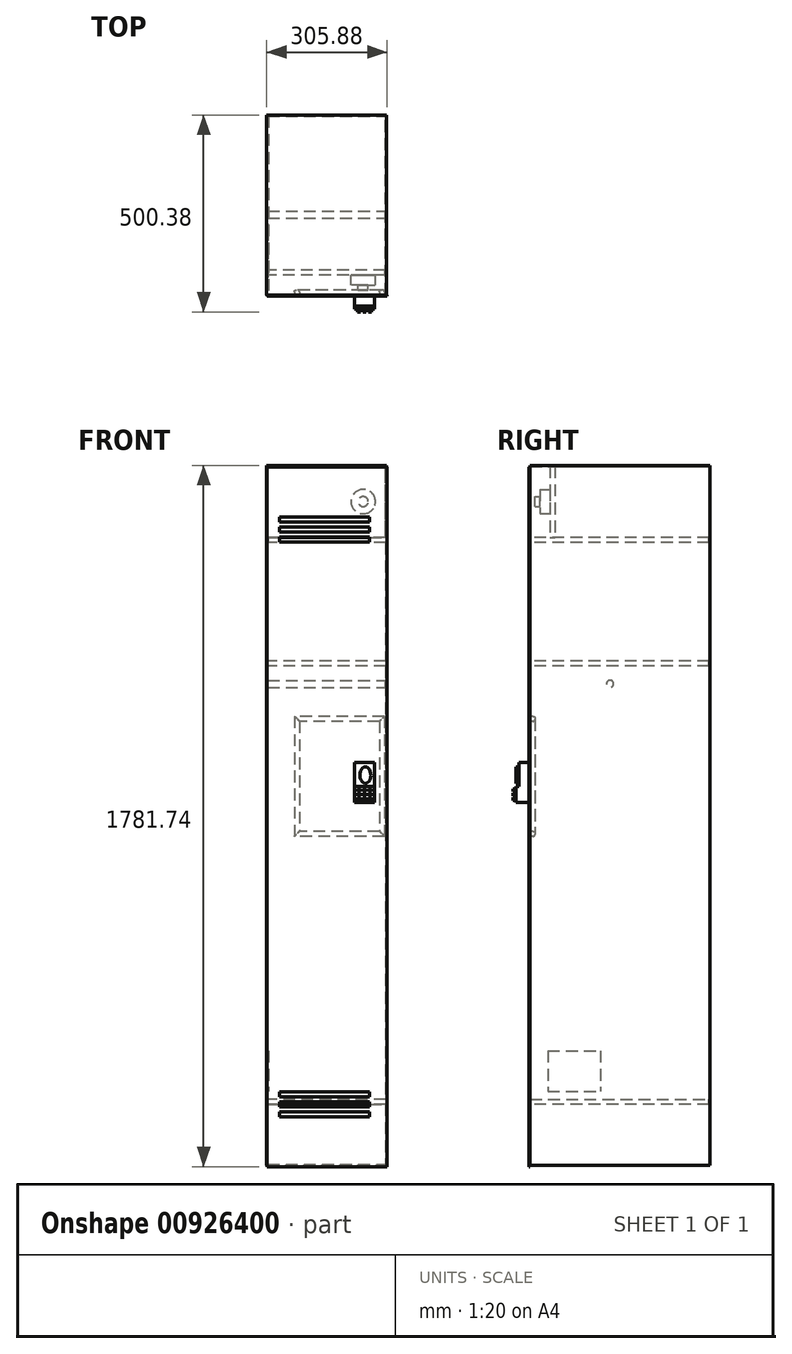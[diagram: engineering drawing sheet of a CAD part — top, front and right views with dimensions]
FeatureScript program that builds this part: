
annotation { "Feature Type Name" : "Feature", "Feature Type Description" : "" }
export const myFeature = defineFeature(function(context is Context, id is Id, definition is map)
    precondition{}
    {
        {
            var Q0;
            Q0=qCreatedBy(makeId("Front.planeOp"),FACE);
            var sketch = newSketch(context, id + "F0", { "sketchPlane" : qUnion([Q0])});
            skLineSegment(sketch, "E0.bottom", {"start": v(-28.78, 1709) * mm, "end": v(276.02, 1709) * mm});
            skLineSegment(sketch, "E0.top", {"start": v(-28.78, -69) * mm, "end": v(276.02, -69) * mm});
            skLineSegment(sketch, "E0.left", {"start": v(-28.78, 1709) * mm, "end": v(-28.78, -69) * mm});
            skLineSegment(sketch, "E0.right", {"start": v(276.02, 1709) * mm, "end": v(276.02, -69) * mm});
            skPoint(sketch, "E1", {"position": v(-28.78, 1709) * mm});
            skPoint(sketch, "E2", {"position": v(-28.78, -69) * mm});
            skSolve(sketch);
        }
        {
            var Q0;
            Q0=qSketchRegion(id+"F0",true);
            extrude(context, id + "F1", {"entities" : qUnion([Q0]), "depth" : 457.2 * mm, "offsetDistance" : 25.4 * mm});
        }
        {
            var Q0;
            Q0=makeQuery(id+"F1.opExtrude","CAP_FACE",FACE,{"disambiguationData":[OSD([sQuery(id+"F0.wireOp",EDGE,"E0.bottom"),sQuery(id+"F0.wireOp",EDGE,"E0.top"),sQuery(id+"F0.wireOp",EDGE,"E0.left"),sQuery(id+"F0.wireOp",EDGE,"E0.right")])],"isStart":false});
            shell(context, id + "F2", {"entities" : qUnion([Q0]), "thickness" : 2.54 * mm});
        }
        {
            var Q0;
            Q0=makeQuery(id+"F2.opShell","OFFSET_FACE",FACE,{"disambiguationData":[OSD([sQuery(id+"F0.wireOp",EDGE,"E0.left")])]});
            var sketch = newSketch(context, id + "F3", { "sketchPlane" : qUnion([Q0])});
            skPoint(sketch, "E3", {"position": v(-457.2, 1706.45) * mm});
            skPoint(sketch, "E4", {"position": v(-457.2, -66.47) * mm});
            skSolve(sketch);
        }
        {
            var Q0;
            Q0=qCreatedBy(makeId("Front.planeOp"),FACE);
            cPlane(context, id + "F4", {"entities" : qUnion([Q0]), "cplaneType" : CPlaneType.OFFSET, "offset" : 457.2 * mm, "width" : 152.4 * mm, "height" : 152.4 * mm});
        }
        {
            var Q0;
            Q0=qCreatedBy(id+"F4.planeOp",FACE);
            var sketch = newSketch(context, id + "F5", { "sketchPlane" : qUnion([Q0])});
            skLineSegment(sketch, "E5.bottom", {"start": v(-26.2, 98.63) * mm, "end": v(273.47, 98.63) * mm});
            skLineSegment(sketch, "E5.top", {"start": v(-26.2, 85.93) * mm, "end": v(273.47, 85.93) * mm});
            skLineSegment(sketch, "E5.left", {"start": v(-26.2, 98.63) * mm, "end": v(-26.2, 85.93) * mm});
            skLineSegment(sketch, "E5.right", {"start": v(273.47, 98.63) * mm, "end": v(273.47, 85.93) * mm});
            skLineSegment(sketch, "E6.bottom", {"start": v(-25, 1211.53) * mm, "end": v(273.53, 1211.53) * mm});
            skLineSegment(sketch, "E6.top", {"start": v(-25, 1198.83) * mm, "end": v(273.53, 1198.83) * mm});
            skLineSegment(sketch, "E6.left", {"start": v(-25, 1211.53) * mm, "end": v(-25, 1198.83) * mm});
            skLineSegment(sketch, "E6.right", {"start": v(273.53, 1211.53) * mm, "end": v(273.53, 1198.83) * mm});
            skLineSegment(sketch, "E7.bottom", {"start": v(-24.41, 1525.34) * mm, "end": v(273.53, 1525.34) * mm});
            skLineSegment(sketch, "E7.top", {"start": v(-24.41, 1512.64) * mm, "end": v(273.53, 1512.64) * mm});
            skLineSegment(sketch, "E7.left", {"start": v(-24.41, 1525.34) * mm, "end": v(-24.41, 1512.64) * mm});
            skLineSegment(sketch, "E7.right", {"start": v(273.53, 1525.34) * mm, "end": v(273.53, 1512.64) * mm});
            skSolve(sketch);
        }
        {
            var Q0;
            Q0=makeQuery(id+"F5.imprint","IMPRINT",FACE,{"disambiguationData":[TD([[makeQuery(id+"F5.imprint","IMPRINT",EDGE,{"derivedFrom":sQuery(id+"F5.wireOp",EDGE,"E5.bottom")}),-1.0]])]});
            var Q1;
            Q1=makeQuery(id+"F5.imprint","IMPRINT",FACE,{"disambiguationData":[TD([[makeQuery(id+"F5.imprint","IMPRINT",EDGE,{"derivedFrom":sQuery(id+"F5.wireOp",EDGE,"VyrBGK2K-1y9x-VAEc-Igx1-qJqO2NATqdDI.bottom")}),-1.0]])]});
            var Q2;
            Q2=makeQuery(id+"F5.imprint","IMPRINT",FACE,{"disambiguationData":[TD([[makeQuery(id+"F5.imprint","IMPRINT",EDGE,{"derivedFrom":sQuery(id+"F5.wireOp",EDGE,"E6.bottom")}),-1.0]])]});
            var Q3;
            Q3=makeQuery(id+"F5.imprint","IMPRINT",FACE,{"disambiguationData":[TD([[makeQuery(id+"F5.imprint","IMPRINT",EDGE,{"derivedFrom":sQuery(id+"F5.wireOp",EDGE,"E7.bottom")}),-1.0]])]});
            extrude(context, id + "F6", {"entities" : qUnion([Q0, Q1, Q2, Q3]), "operationType" : NewBodyOperationType.ADD, "endBound" : BoundingType.UP_TO_NEXT, "oppositeDirection" : true, "depth" : 25.4 * mm, "offsetDistance" : 25.4 * mm});
        }
        {
            var Q0;
            Q0=makeQuery(id+"F6.boolean.opBoolean","MERGE",FACE,{"derivedFrom":[makeQuery(id+"F1.opExtrude","CAP_FACE",FACE,{"disambiguationData":[OSD([sQuery(id+"F0.wireOp",EDGE,"E0.bottom"),sQuery(id+"F0.wireOp",EDGE,"E0.top"),sQuery(id+"F0.wireOp",EDGE,"E0.left"),sQuery(id+"F0.wireOp",EDGE,"E0.right")])],"isStart":false}),makeQuery(id+"F6.opExtrude","CAP_FACE",FACE,{"disambiguationData":[OSD([sQuery(id+"F5.wireOp",EDGE,"E5.bottom"),sQuery(id+"F5.wireOp",EDGE,"E5.top"),sQuery(id+"F5.wireOp",EDGE,"E5.left"),sQuery(id+"F5.wireOp",EDGE,"E5.right")])],"isStart":true}),makeQuery(id+"F6.opExtrude","CAP_FACE",FACE,{"disambiguationData":[OSD([sQuery(id+"F5.wireOp",EDGE,"E6.bottom"),sQuery(id+"F5.wireOp",EDGE,"E6.top"),sQuery(id+"F5.wireOp",EDGE,"E6.left"),sQuery(id+"F5.wireOp",EDGE,"E6.right")])],"isStart":true}),makeQuery(id+"F6.opExtrude","CAP_FACE",FACE,{"disambiguationData":[OSD([sQuery(id+"F5.wireOp",EDGE,"E7.bottom"),sQuery(id+"F5.wireOp",EDGE,"E7.top"),sQuery(id+"F5.wireOp",EDGE,"E7.left"),sQuery(id+"F5.wireOp",EDGE,"E7.right")])],"isStart":true})]});
            var sketch = newSketch(context, id + "F7", { "sketchPlane" : qUnion([Q0])});
            skPoint(sketch, "E8", {"position": v(-25, 1198.83) * mm});
            skPoint(sketch, "E9", {"position": v(273.48, 1198.83) * mm});
            skPoint(sketch, "E10", {"position": v(124.24, 1198.83) * mm});
            skSolve(sketch);
        }
        {
            var Q0;
            {var subQ7=sQuery(id+"F0.wireOp",EDGE,"E0.bottom");var subQ8=makeQuery(id+"F1.opExtrude","CAP_EDGE",EDGE,{"disambiguationData":[OSD([subQ7])],"isStart":false});Q0=makeQuery(id+"F7.imprint","IMPRINT",FACE,{"disambiguationData":[TD([[makeQuery(id+"F7.imprint","IMPRINT",EDGE,{"derivedFrom":subQ8}),-1.0]])]});}
            cPlane(context, id + "F8", {"entities" : qUnion([Q0]), "cplaneType" : CPlaneType.OFFSET, "offset" : 0 * mm, "width" : 152.4 * mm, "height" : 152.4 * mm});
        }
        {
            var Q0;
            Q0=qCreatedBy(id+"F8.planeOp",FACE);
            var sketch = newSketch(context, id + "F9", { "sketchPlane" : qUnion([Q0])});
            skLineSegment(sketch, "E11.bottom", {"start": v(-27.7, 1705.25) * mm, "end": v(277.1, 1705.25) * mm});
            skLineSegment(sketch, "E11.top", {"start": v(-27.7, -72.75) * mm, "end": v(277.1, -72.75) * mm});
            skLineSegment(sketch, "E11.left", {"start": v(-27.7, 1705.25) * mm, "end": v(-27.7, -72.75) * mm});
            skLineSegment(sketch, "E11.right", {"start": v(277.1, 1705.25) * mm, "end": v(277.1, -72.75) * mm});
            skLineSegment(sketch, "E12.bottom", {"start": v(3.97, 1578.25) * mm, "end": v(232.57, 1578.25) * mm});
            skLineSegment(sketch, "E12.top", {"start": v(3.97, 1565.55) * mm, "end": v(232.57, 1565.55) * mm});
            skLineSegment(sketch, "E12.left", {"start": v(3.97, 1578.25) * mm, "end": v(3.97, 1565.55) * mm});
            skLineSegment(sketch, "E12.right", {"start": v(232.57, 1578.25) * mm, "end": v(232.57, 1565.55) * mm});
            skLineSegment(sketch, "E13.bottom", {"start": v(232.57, 1552.85) * mm, "end": v(3.97, 1552.85) * mm});
            skLineSegment(sketch, "E13.top", {"start": v(232.57, 1540.15) * mm, "end": v(3.97, 1540.15) * mm});
            skLineSegment(sketch, "E13.left", {"start": v(232.57, 1552.85) * mm, "end": v(232.57, 1540.15) * mm});
            skLineSegment(sketch, "E13.right", {"start": v(3.97, 1552.85) * mm, "end": v(3.97, 1540.15) * mm});
            skLineSegment(sketch, "E14.bottom", {"start": v(232.57, 1527.45) * mm, "end": v(3.97, 1527.45) * mm});
            skLineSegment(sketch, "E14.top", {"start": v(232.57, 1514.75) * mm, "end": v(3.97, 1514.75) * mm});
            skLineSegment(sketch, "E14.left", {"start": v(232.57, 1527.45) * mm, "end": v(232.57, 1514.75) * mm});
            skLineSegment(sketch, "E14.right", {"start": v(3.97, 1527.45) * mm, "end": v(3.97, 1514.75) * mm});
            skLineSegment(sketch, "E15", {"start": v(203.5, -72.75) * mm, "end": v(203.5, 816.25) * mm, "construction": true});
            skLineSegment(sketch, "E16", {"start": v(277.1, 816.25) * mm, "end": v(-27.7, 816.25) * mm, "construction": true});
            skLineSegment(sketch, "E17.MirrorCS", {"start": v(232.57, 117.75) * mm, "end": v(3.97, 117.75) * mm});
            skLineSegment(sketch, "E18.MirrorCS", {"start": v(232.57, 105.05) * mm, "end": v(3.97, 105.05) * mm});
            skLineSegment(sketch, "E19.MirrorCS", {"start": v(232.57, 92.35) * mm, "end": v(3.97, 92.35) * mm});
            skLineSegment(sketch, "E20.MirrorCS", {"start": v(232.57, 79.65) * mm, "end": v(3.97, 79.65) * mm});
            skLineSegment(sketch, "E21.MirrorCS", {"start": v(3.97, 66.95) * mm, "end": v(232.57, 66.95) * mm});
            skLineSegment(sketch, "E22.MirrorCS", {"start": v(3.97, 54.25) * mm, "end": v(232.57, 54.25) * mm});
            skLineSegment(sketch, "E23.MirrorCS", {"start": v(3.97, 54.25) * mm, "end": v(3.97, 66.95) * mm});
            skLineSegment(sketch, "E24.MirrorCS", {"start": v(3.97, 79.65) * mm, "end": v(3.97, 92.35) * mm});
            skLineSegment(sketch, "E25.MirrorCS", {"start": v(3.97, 105.05) * mm, "end": v(3.97, 117.75) * mm});
            skLineSegment(sketch, "E26.MirrorCS", {"start": v(232.57, 105.05) * mm, "end": v(232.57, 117.75) * mm});
            skLineSegment(sketch, "E27.MirrorCS", {"start": v(232.57, 79.65) * mm, "end": v(232.57, 92.35) * mm});
            skLineSegment(sketch, "E28.MirrorCS", {"start": v(232.57, 54.25) * mm, "end": v(232.57, 66.95) * mm});
            skLineSegment(sketch, "E29", {"start": v(174.02, 54.25) * mm, "end": v(174.02, -72.75) * mm, "construction": true});
            skSolve(sketch);
        }
        {
            var Q0;
            Q0=makeQuery(id+"F9.imprint","IMPRINT",FACE,{"disambiguationData":[TD([[makeQuery(id+"F9.imprint","IMPRINT",EDGE,{"derivedFrom":sQuery(id+"F9.wireOp",EDGE,"E11.bottom")}),-1.0]])]});
            extrude(context, id + "F10", {"entities" : qUnion([Q0]), "operationType" : NewBodyOperationType.ADD, "depth" : 2.54 * mm, "offsetDistance" : 25.4 * mm});
        }
        {
            var Q0;
            Q0=makeQuery(id+"F10.opExtrude","CAP_FACE",FACE,{"disambiguationData":[OSD([sQuery(id+"F9.wireOp",EDGE,"E11.bottom"),sQuery(id+"F9.wireOp",EDGE,"E11.top"),sQuery(id+"F9.wireOp",EDGE,"E11.left"),sQuery(id+"F9.wireOp",EDGE,"E11.right"),sQuery(id+"F9.wireOp",EDGE,"E12.bottom"),sQuery(id+"F9.wireOp",EDGE,"E12.top"),sQuery(id+"F9.wireOp",EDGE,"E12.left"),sQuery(id+"F9.wireOp",EDGE,"E12.right"),sQuery(id+"F9.wireOp",EDGE,"E13.bottom"),sQuery(id+"F9.wireOp",EDGE,"E13.top"),sQuery(id+"F9.wireOp",EDGE,"E13.left"),sQuery(id+"F9.wireOp",EDGE,"E13.right"),sQuery(id+"F9.wireOp",EDGE,"E14.bottom"),sQuery(id+"F9.wireOp",EDGE,"E14.top"),sQuery(id+"F9.wireOp",EDGE,"E14.left"),sQuery(id+"F9.wireOp",EDGE,"E14.right")])],"isStart":false});
            var sketch = newSketch(context, id + "F11", { "sketchPlane" : qUnion([Q0])});
            skLineSegment(sketch, "E30.bottom", {"start": v(195, 953.76) * mm, "end": v(245.8, 953.76) * mm});
            skLineSegment(sketch, "E30.top", {"start": v(195, 852.16) * mm, "end": v(245.8, 852.16) * mm});
            skLineSegment(sketch, "E30.left", {"start": v(195, 953.76) * mm, "end": v(195, 852.16) * mm});
            skLineSegment(sketch, "E30.right", {"start": v(245.8, 953.76) * mm, "end": v(245.8, 852.16) * mm});
            skSolve(sketch);
        }
        {
            var Q0;
            Q0=makeQuery(id+"F11.imprint","IMPRINT",FACE,{"disambiguationData":[TD([[makeQuery(id+"F11.imprint","IMPRINT",EDGE,{"derivedFrom":sQuery(id+"F11.wireOp",EDGE,"E30.bottom")}),-1.0]])]});
            extrude(context, id + "F12", {"entities" : qUnion([Q0]), "operationType" : NewBodyOperationType.ADD, "depth" : 25.4 * mm, "offsetDistance" : 25.4 * mm});
        }
        {
            var Q0;
            {var subQ0=sQuery(id+"F5.wireOp",EDGE,"E5.bottom");var subQ1=sQuery(id+"F0.wireOp",EDGE,"E0.right");Q0=makeQuery(id+"F6.boolean.opBoolean","SPLIT",FACE,{"disambiguationData":[TD([makeQuery(id+"F6.opExtrude","SWEPT_FACE",FACE,{"disambiguationData":[OSD([subQ0])]})])],"derivedFrom":makeQuery(id+"F2.opShell","OFFSET_FACE",FACE,{"disambiguationData":[OSD([subQ1])]})});}
            var sketch = newSketch(context, id + "F13", { "sketchPlane" : qUnion([Q0])});
            skCircle(sketch, "E31", {"center": v(253.8, 1154.02) * mm, "radius": 8.9 * mm});
            skSolve(sketch);
        }
        {
            var Q0;
            Q0=makeQuery(id+"F13.imprint","IMPRINT",FACE,{"disambiguationData":[TD([[makeQuery(id+"F13.imprint","IMPRINT",EDGE,{"derivedFrom":sQuery(id+"F13.wireOp",EDGE,"E31")}),1.0]])]});
            extrude(context, id + "F14", {"entities" : qUnion([Q0]), "operationType" : NewBodyOperationType.ADD, "endBound" : BoundingType.UP_TO_NEXT, "depth" : 25.4 * mm, "offsetDistance" : 25.4 * mm});
        }
        {
            var Q0;
            Q0=makeQuery(id+"F10.opExtrude","CAP_FACE",FACE,{"disambiguationData":[OSD([sQuery(id+"F9.wireOp",EDGE,"E11.bottom"),sQuery(id+"F9.wireOp",EDGE,"E11.top"),sQuery(id+"F9.wireOp",EDGE,"E11.left"),sQuery(id+"F9.wireOp",EDGE,"E11.right"),sQuery(id+"F9.wireOp",EDGE,"E12.bottom"),sQuery(id+"F9.wireOp",EDGE,"E12.top"),sQuery(id+"F9.wireOp",EDGE,"E12.left"),sQuery(id+"F9.wireOp",EDGE,"E12.right"),sQuery(id+"F9.wireOp",EDGE,"E13.bottom"),sQuery(id+"F9.wireOp",EDGE,"E13.top"),sQuery(id+"F9.wireOp",EDGE,"E13.left"),sQuery(id+"F9.wireOp",EDGE,"E13.right"),sQuery(id+"F9.wireOp",EDGE,"E14.bottom"),sQuery(id+"F9.wireOp",EDGE,"E14.top"),sQuery(id+"F9.wireOp",EDGE,"E14.left"),sQuery(id+"F9.wireOp",EDGE,"E14.right"),sQuery(id+"F9.wireOp",EDGE,"E17.MirrorCS"),sQuery(id+"F9.wireOp",EDGE,"E18.MirrorCS"),sQuery(id+"F9.wireOp",EDGE,"E19.MirrorCS"),sQuery(id+"F9.wireOp",EDGE,"E20.MirrorCS"),sQuery(id+"F9.wireOp",EDGE,"E21.MirrorCS"),sQuery(id+"F9.wireOp",EDGE,"E22.MirrorCS"),sQuery(id+"F9.wireOp",EDGE,"E23.MirrorCS"),sQuery(id+"F9.wireOp",EDGE,"E24.MirrorCS"),sQuery(id+"F9.wireOp",EDGE,"E25.MirrorCS"),sQuery(id+"F9.wireOp",EDGE,"E26.MirrorCS"),sQuery(id+"F9.wireOp",EDGE,"E27.MirrorCS"),sQuery(id+"F9.wireOp",EDGE,"E28.MirrorCS")])],"isStart":true});
            var sketch = newSketch(context, id + "F15", { "sketchPlane" : qUnion([Q0])});
            skLineSegment(sketch, "E32.bottom", {"start": v(-270.4, 1071.45) * mm, "end": v(-41.8, 1071.45) * mm});
            skLineSegment(sketch, "E32.top", {"start": v(-270.4, 766.65) * mm, "end": v(-41.8, 766.65) * mm});
            skLineSegment(sketch, "E32.left", {"start": v(-270.4, 1071.45) * mm, "end": v(-270.4, 766.65) * mm});
            skLineSegment(sketch, "E32.right", {"start": v(-41.8, 1071.45) * mm, "end": v(-41.8, 766.65) * mm});
            skLineSegment(sketch, "E33.0", {"start": v(-257.7, 1058.75) * mm, "end": v(-54.5, 1058.75) * mm});
            skLineSegment(sketch, "E33.1", {"start": v(-257.7, 1058.75) * mm, "end": v(-257.7, 779.35) * mm});
            skLineSegment(sketch, "E33.2", {"start": v(-257.7, 779.35) * mm, "end": v(-54.5, 779.35) * mm});
            skLineSegment(sketch, "E33.3", {"start": v(-54.5, 1058.75) * mm, "end": v(-54.5, 779.35) * mm});
            skSolve(sketch);
        }
        {
            var Q0;
            Q0=makeQuery(id+"F15.imprint","IMPRINT",FACE,{"disambiguationData":[TD([[makeQuery(id+"F15.imprint","IMPRINT",EDGE,{"derivedFrom":sQuery(id+"F15.wireOp",EDGE,"E32.bottom")}),-1.0]])]});
            extrude(context, id + "F16", {"entities" : qUnion([Q0]), "operationType" : NewBodyOperationType.ADD, "depth" : 12.7 * mm, "offsetDistance" : 25.4 * mm});
        }
        {
            var Q0;
            Q0=makeQuery(id+"F16.opExtrude","CAP_EDGE",EDGE,{"disambiguationData":[OSD([sQuery(id+"F15.wireOp",EDGE,"E32.left")])],"isStart":false});
            var Q1;
            Q1=makeQuery(id+"F16.opExtrude","CAP_EDGE",EDGE,{"disambiguationData":[OSD([sQuery(id+"F15.wireOp",EDGE,"E32.bottom")])],"isStart":false});
            var Q2;
            Q2=makeQuery(id+"F16.opExtrude","CAP_EDGE",EDGE,{"disambiguationData":[OSD([sQuery(id+"F15.wireOp",EDGE,"E32.right")])],"isStart":false});
            var Q3;
            Q3=makeQuery(id+"F16.opExtrude","CAP_EDGE",EDGE,{"disambiguationData":[OSD([sQuery(id+"F15.wireOp",EDGE,"E32.top")])],"isStart":false});
            var Q4;
            Q4=makeQuery(id+"F16.opExtrude","CAP_EDGE",EDGE,{"disambiguationData":[OSD([sQuery(id+"F15.wireOp",EDGE,"E33.2")])],"isStart":false});
            var Q5;
            Q5=makeQuery(id+"F16.opExtrude","CAP_EDGE",EDGE,{"disambiguationData":[OSD([sQuery(id+"F15.wireOp",EDGE,"E33.3")])],"isStart":false});
            var Q6;
            Q6=makeQuery(id+"F16.opExtrude","CAP_EDGE",EDGE,{"disambiguationData":[OSD([sQuery(id+"F15.wireOp",EDGE,"E33.1")])],"isStart":false});
            var Q7;
            Q7=makeQuery(id+"F16.opExtrude","CAP_EDGE",EDGE,{"disambiguationData":[OSD([sQuery(id+"F15.wireOp",EDGE,"E33.0")])],"isStart":false});
            fillet(context, id + "F17", {"entities" : qUnion([Q0, Q1, Q2, Q3, Q4, Q5, Q6, Q7]), "radius" : 5.08 * mm, "tangentPropagation" : true, "allowEdgeOverflow" : false});
        }
        {
            var Q0;
            {var subQ0=sQuery(id+"F0.wireOp",EDGE,"E0.left");Q0=makeQuery(id+"F3.imprint","IMPRINT",FACE,{"disambiguationData":[TD([[makeQuery(id+"F3.imprint","IMPRINT",EDGE,{"derivedFrom":makeQuery(id+"F2.opShell","OFFSET_EDGE",EDGE,{"disambiguationData":[OSD([subQ0]),TDD([makeQuery(id+"F1.opExtrude","CAP_EDGE",EDGE,{"disambiguationData":[OSD([subQ0])],"isStart":true})])]})}),-1.0]])]});}
            var sketch = newSketch(context, id + "F18", { "sketchPlane" : qUnion([Q0])});
            skLineSegment(sketch, "E34.bottom", {"start": v(-406.4, 1707.77) * mm, "end": v(-393.7, 1707.77) * mm});
            skLineSegment(sketch, "E34.top", {"start": v(-406.4, 1525.9) * mm, "end": v(-393.7, 1525.9) * mm});
            skLineSegment(sketch, "E34.left", {"start": v(-406.4, 1707.77) * mm, "end": v(-406.4, 1525.9) * mm});
            skLineSegment(sketch, "E34.right", {"start": v(-393.7, 1707.77) * mm, "end": v(-393.7, 1525.9) * mm});
            skSolve(sketch);
        }
        {
            var Q0;
            {var subQ0=sQuery(id+"F18.wireOp",EDGE,"E34.top");Q0=makeQuery(id+"F18.imprint","IMPRINT",FACE,{"disambiguationData":[TD([[makeQuery(id+"F18.imprint","IMPRINT",EDGE,{"derivedFrom":subQ0}),1.0]])]});}
            extrude(context, id + "F19", {"entities" : qUnion([Q0]), "operationType" : NewBodyOperationType.ADD, "depth" : 298.53 * mm, "offsetDistance" : 25.4 * mm});
        }
        {
            var Q0;
            Q0=makeQuery(id+"F19.opExtrude","SWEPT_FACE",FACE,{"disambiguationData":[OSD([sQuery(id+"F18.wireOp",EDGE,"E34.left")])]});
            var sketch = newSketch(context, id + "F20", { "sketchPlane" : qUnion([Q0])});
            skCircle(sketch, "E35", {"center": v(216.47, 1616.96) * mm, "radius": 31.03 * mm});
            skSolve(sketch);
        }
        {
            var Q0;
            Q0=makeQuery(id+"F20.imprint","IMPRINT",FACE,{"disambiguationData":[TD([[makeQuery(id+"F20.imprint","IMPRINT",EDGE,{"derivedFrom":sQuery(id+"F20.wireOp",EDGE,"E35")}),1.0]])]});
            extrude(context, id + "F21", {"entities" : qUnion([Q0]), "operationType" : NewBodyOperationType.ADD, "depth" : 25.4 * mm, "offsetDistance" : 25.4 * mm});
        }
        {
            var Q0;
            Q0=makeQuery(id+"F21.opExtrude","CAP_FACE",FACE,{"disambiguationData":[OSD([sQuery(id+"F20.wireOp",EDGE,"E35")])],"isStart":false});
            var sketch = newSketch(context, id + "F22", { "sketchPlane" : qUnion([Q0])});
            skCircle(sketch, "E36", {"center": v(216.47, 1616.96) * mm, "radius": 12.7 * mm});
            skSolve(sketch);
        }
        {
            var Q0;
            Q0=makeQuery(id+"F22.imprint","IMPRINT",FACE,{"disambiguationData":[TD([[makeQuery(id+"F22.imprint","IMPRINT",EDGE,{"derivedFrom":sQuery(id+"F22.wireOp",EDGE,"E36")}),1.0]])]});
            extrude(context, id + "F23", {"entities" : qUnion([Q0]), "operationType" : NewBodyOperationType.ADD, "depth" : 12.7 * mm, "offsetDistance" : 25.4 * mm});
        }
        {
            var Q0;
            Q0=makeQuery(id+"F12.opExtrude","CAP_FACE",FACE,{"disambiguationData":[OSD([sQuery(id+"F11.wireOp",EDGE,"E30.bottom"),sQuery(id+"F11.wireOp",EDGE,"E30.top"),sQuery(id+"F11.wireOp",EDGE,"E30.left"),sQuery(id+"F11.wireOp",EDGE,"E30.right")])],"isStart":false});
            var sketch = newSketch(context, id + "F24", { "sketchPlane" : qUnion([Q0])});
            skEllipse(sketch, "E37", {"center": v(221.9, 922.19) * mm, "majorRadius": 21.07 * mm, "minorRadius": 13.97 * mm, "majorAxis": v(0, 1)});
            skLineSegment(sketch, "E38.bottom", {"start": v(195, 893.4) * mm, "end": v(245.8, 893.4) * mm});
            skLineSegment(sketch, "E38.top", {"start": v(195, 852.16) * mm, "end": v(245.8, 852.16) * mm});
            skLineSegment(sketch, "E38.left", {"start": v(195, 893.4) * mm, "end": v(195, 852.16) * mm});
            skLineSegment(sketch, "E38.right", {"start": v(245.8, 893.4) * mm, "end": v(245.8, 852.16) * mm});
            skSolve(sketch);
        }
        {
            var Q0;
            Q0=makeQuery(id+"F24.imprint","IMPRINT",FACE,{"disambiguationData":[TD([[makeQuery(id+"F24.imprint","IMPRINT",EDGE,{"derivedFrom":sQuery(id+"F24.wireOp",EDGE,"E37")}),1.0]])]});
            var Q1;
            Q1=makeQuery(id+"F24.imprint","IMPRINT",FACE,{"disambiguationData":[TD([[makeQuery(id+"F24.imprint","IMPRINT",EDGE,{"derivedFrom":sQuery(id+"F24.wireOp",EDGE,"E38.bottom")}),-1.0]])]});
            extrude(context, id + "F25", {"entities" : qUnion([Q0, Q1]), "operationType" : NewBodyOperationType.ADD, "depth" : 7.62 * mm, "offsetDistance" : 25.4 * mm});
        }
        {
            var Q0;
            {var subQ0=sQuery(id+"F0.wireOp",EDGE,"E0.left");Q0=makeQuery(id+"F3.imprint","IMPRINT",FACE,{"disambiguationData":[TD([[makeQuery(id+"F3.imprint","IMPRINT",EDGE,{"derivedFrom":makeQuery(id+"F2.opShell","OFFSET_EDGE",EDGE,{"disambiguationData":[OSD([subQ0]),TDD([makeQuery(id+"F1.opExtrude","CAP_EDGE",EDGE,{"disambiguationData":[OSD([subQ0])],"isStart":true})])]})}),-1.0]])]});}
            var sketch = newSketch(context, id + "F26", { "sketchPlane" : qUnion([Q0])});
            skLineSegment(sketch, "E39.bottom", {"start": v(-411.97, 221.7) * mm, "end": v(-278.8, 221.7) * mm});
            skLineSegment(sketch, "E39.top", {"start": v(-411.97, 118.67) * mm, "end": v(-278.8, 118.67) * mm});
            skLineSegment(sketch, "E39.left", {"start": v(-411.97, 221.7) * mm, "end": v(-411.97, 118.67) * mm});
            skLineSegment(sketch, "E39.right", {"start": v(-278.8, 221.7) * mm, "end": v(-278.8, 118.67) * mm});
            skSolve(sketch);
        }
        {
            var Q0;
            Q0=makeQuery(id+"F26.imprint","IMPRINT",FACE,{"disambiguationData":[TD([[makeQuery(id+"F26.imprint","IMPRINT",EDGE,{"derivedFrom":sQuery(id+"F26.wireOp",EDGE,"E39.bottom")}),-1.0]])]});
            extrude(context, id + "F27", {"entities" : qUnion([Q0]), "operationType" : NewBodyOperationType.ADD, "depth" : 2.54 * mm, "offsetDistance" : 25.4 * mm});
        }
        {
            var Q0;
            Q0=makeQuery(id+"F25.opExtrude","CAP_FACE",FACE,{"disambiguationData":[OSD([sQuery(id+"F24.wireOp",EDGE,"E38.bottom"),sQuery(id+"F24.wireOp",EDGE,"E38.top"),sQuery(id+"F24.wireOp",EDGE,"E38.left"),sQuery(id+"F24.wireOp",EDGE,"E38.right")])],"isStart":false});
            var sketch = newSketch(context, id + "F28", { "sketchPlane" : qUnion([Q0])});
            skLineSegment(sketch, "E40.bottom", {"start": v(202.5, 887.3) * mm, "end": v(209.96, 887.3) * mm});
            skLineSegment(sketch, "E40.top", {"start": v(202.5, 879.84) * mm, "end": v(209.96, 879.84) * mm});
            skLineSegment(sketch, "E40.left", {"start": v(202.5, 887.3) * mm, "end": v(202.5, 879.84) * mm});
            skLineSegment(sketch, "E40.right", {"start": v(209.96, 887.3) * mm, "end": v(209.96, 879.84) * mm});
            skLineSegment(sketch, "E41", {"start": v(213.04, 894.08) * mm, "end": v(213.04, 878.08) * mm, "construction": true});
            skLineSegment(sketch, "E42.MirrorCS", {"start": v(223.57, 879.84) * mm, "end": v(216.1, 879.84) * mm});
            skLineSegment(sketch, "E43.MirrorCS", {"start": v(216.1, 887.3) * mm, "end": v(216.1, 879.84) * mm});
            skLineSegment(sketch, "E44.MirrorCS", {"start": v(223.57, 887.3) * mm, "end": v(216.1, 887.3) * mm});
            skLineSegment(sketch, "E45.MirrorCS", {"start": v(223.57, 887.3) * mm, "end": v(223.57, 879.84) * mm});
            skLineSegment(sketch, "E46", {"start": v(226.86, 888.62) * mm, "end": v(226.86, 856.8) * mm, "construction": true});
            skLineSegment(sketch, "E47.MirrorCS", {"start": v(230.15, 887.3) * mm, "end": v(237.61, 887.3) * mm});
            skLineSegment(sketch, "E48.MirrorCS", {"start": v(230.15, 887.3) * mm, "end": v(230.15, 879.84) * mm});
            skLineSegment(sketch, "E49.MirrorCS", {"start": v(230.15, 879.84) * mm, "end": v(237.61, 879.84) * mm});
            skLineSegment(sketch, "E50.MirrorCS", {"start": v(237.61, 887.3) * mm, "end": v(237.61, 879.84) * mm});
            skLineSegment(sketch, "E51", {"start": v(556.5, 878.08) * mm, "end": v(213.04, 878.08) * mm, "construction": true});
            skLineSegment(sketch, "E52.MirrorCS", {"start": v(202.5, 876.33) * mm, "end": v(209.96, 876.33) * mm});
            skLineSegment(sketch, "E53.MirrorCS", {"start": v(209.96, 868.87) * mm, "end": v(209.96, 876.33) * mm});
            skLineSegment(sketch, "E54.MirrorCS", {"start": v(202.5, 868.87) * mm, "end": v(209.96, 868.87) * mm});
            skLineSegment(sketch, "E55.MirrorCS", {"start": v(202.5, 868.87) * mm, "end": v(202.5, 876.33) * mm});
            skLineSegment(sketch, "E56.MirrorCS", {"start": v(213.04, 862.09) * mm, "end": v(213.04, 878.08) * mm, "construction": true});
            skLineSegment(sketch, "E57.MirrorCS", {"start": v(223.57, 868.87) * mm, "end": v(216.1, 868.87) * mm});
            skLineSegment(sketch, "E58.MirrorCS", {"start": v(223.57, 868.87) * mm, "end": v(223.57, 876.33) * mm});
            skLineSegment(sketch, "E59.MirrorCS", {"start": v(216.1, 868.87) * mm, "end": v(216.1, 876.33) * mm});
            skLineSegment(sketch, "E60.MirrorCS", {"start": v(223.57, 876.33) * mm, "end": v(216.1, 876.33) * mm});
            skLineSegment(sketch, "E61.MirrorCS", {"start": v(230.15, 868.87) * mm, "end": v(230.15, 876.33) * mm});
            skLineSegment(sketch, "E62.MirrorCS", {"start": v(230.15, 876.33) * mm, "end": v(237.61, 876.33) * mm});
            skLineSegment(sketch, "E63.MirrorCS", {"start": v(237.61, 868.87) * mm, "end": v(237.61, 876.33) * mm});
            skLineSegment(sketch, "E64.MirrorCS", {"start": v(230.15, 868.87) * mm, "end": v(237.61, 868.87) * mm});
            skLineSegment(sketch, "E65", {"start": v(556.29, 867.11) * mm, "end": v(213.04, 867.11) * mm, "construction": true});
            skLineSegment(sketch, "E66.MirrorCS", {"start": v(202.5, 865.36) * mm, "end": v(202.5, 857.9) * mm});
            skLineSegment(sketch, "E67.MirrorCS", {"start": v(202.5, 857.9) * mm, "end": v(209.96, 857.9) * mm});
            skLineSegment(sketch, "E68.MirrorCS", {"start": v(209.96, 865.36) * mm, "end": v(209.96, 857.9) * mm});
            skLineSegment(sketch, "E69.MirrorCS", {"start": v(202.5, 865.36) * mm, "end": v(209.96, 865.36) * mm});
            skLineSegment(sketch, "E70.MirrorCS", {"start": v(223.57, 857.9) * mm, "end": v(216.1, 857.9) * mm});
            skLineSegment(sketch, "E71.MirrorCS", {"start": v(223.57, 865.36) * mm, "end": v(223.57, 857.9) * mm});
            skLineSegment(sketch, "E72.MirrorCS", {"start": v(216.1, 865.36) * mm, "end": v(216.1, 857.9) * mm});
            skLineSegment(sketch, "E73.MirrorCS", {"start": v(223.57, 865.36) * mm, "end": v(216.1, 865.36) * mm});
            skLineSegment(sketch, "E74.MirrorCS", {"start": v(237.61, 865.36) * mm, "end": v(237.61, 857.9) * mm});
            skLineSegment(sketch, "E75.MirrorCS", {"start": v(230.15, 857.9) * mm, "end": v(237.61, 857.9) * mm});
            skLineSegment(sketch, "E76.MirrorCS", {"start": v(230.15, 865.36) * mm, "end": v(237.61, 865.36) * mm});
            skLineSegment(sketch, "E77.MirrorCS", {"start": v(230.15, 865.36) * mm, "end": v(230.15, 857.9) * mm});
            skSolve(sketch);
        }
        {
            var Q0;
            Q0=qSketchRegion(id+"F28",true);
            extrude(context, id + "F29", {"entities" : qUnion([Q0]), "operationType" : NewBodyOperationType.ADD, "depth" : 7.62 * mm, "offsetDistance" : 25.4 * mm});
        }
    });
